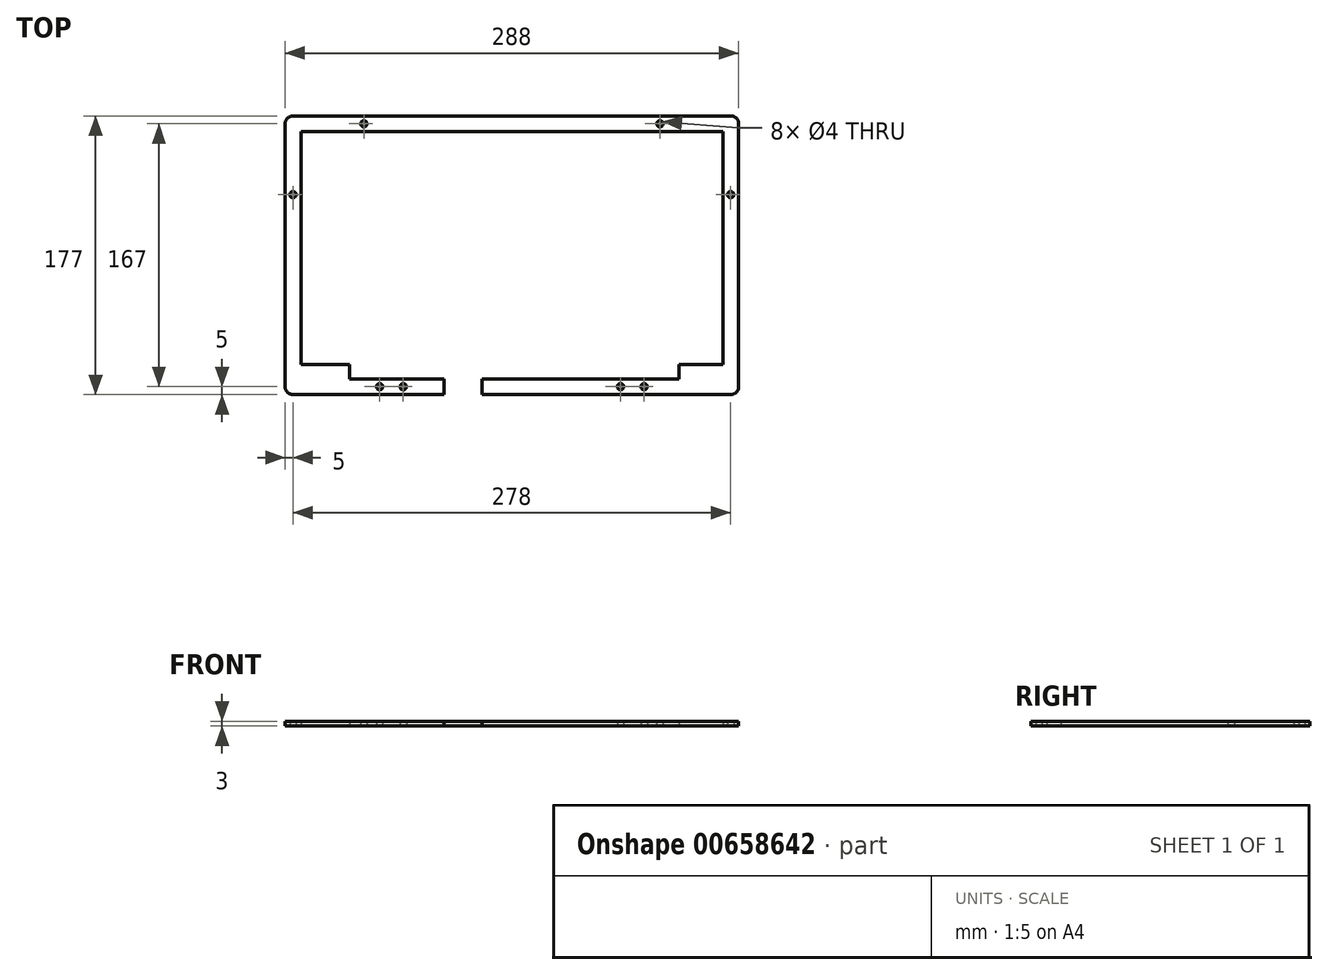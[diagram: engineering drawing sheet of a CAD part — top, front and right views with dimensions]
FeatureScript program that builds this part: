
annotation { "Feature Type Name" : "Feature", "Feature Type Description" : "" }
export const myFeature = defineFeature(function(context is Context, id is Id, definition is map)
    precondition{}
    {
        {
            var Q0;
            Q0=qCreatedBy(makeId("Top.planeOp"),FACE);
            var sketch = newSketch(context, id + "F0", { "sketchPlane" : qUnion([Q0])});
            skLineSegment(sketch, "E0.bottom", {"start": v(-144, 96) * mm, "end": v(144, 96) * mm});
            skLineSegment(sketch, "E0.top", {"start": v(-144, -81) * mm, "end": v(144, -81) * mm});
            skLineSegment(sketch, "E0.left", {"start": v(-144, 96) * mm, "end": v(-144, -81) * mm});
            skLineSegment(sketch, "E0.right", {"start": v(144, 96) * mm, "end": v(144, -81) * mm});
            skCircle(sketch, "E1", {"center": v(-94, 91) * mm, "radius": 2 * mm});
            skCircle(sketch, "E2", {"center": v(-139, 46) * mm, "radius": 2 * mm});
            skCircle(sketch, "E3", {"center": v(94, 91) * mm, "radius": 2 * mm});
            skCircle(sketch, "E4", {"center": v(139, 46) * mm, "radius": 2 * mm});
            skCircle(sketch, "E5", {"center": v(-84, -76) * mm, "radius": 2 * mm});
            skCircle(sketch, "E6", {"center": v(-69, -76) * mm, "radius": 2 * mm});
            skCircle(sketch, "E7", {"center": v(84, -76) * mm, "radius": 2 * mm});
            skCircle(sketch, "E8", {"center": v(69, -76) * mm, "radius": 2 * mm});
            skLineSegment(sketch, "E9.bottom", {"start": v(-134, 86) * mm, "end": v(134, 86) * mm});
            skLineSegment(sketch, "E9.left", {"start": v(-134, 86) * mm, "end": v(-134, -62) * mm});
            skLineSegment(sketch, "E9.right", {"start": v(134, 86) * mm, "end": v(134, -62) * mm});
            skLineSegment(sketch, "E10", {"start": v(-134, -62) * mm, "end": v(-103, -62) * mm});
            skLineSegment(sketch, "E11", {"start": v(134, -62) * mm, "end": v(106, -62) * mm});
            skLineSegment(sketch, "E12", {"start": v(-103, -62) * mm, "end": v(-103, -71) * mm});
            skLineSegment(sketch, "E13", {"start": v(-103, -71) * mm, "end": v(-43, -71) * mm});
            skLineSegment(sketch, "E14", {"start": v(-43, -71) * mm, "end": v(-43, -81) * mm});
            skLineSegment(sketch, "E15", {"start": v(106, -62) * mm, "end": v(106, -71) * mm});
            skLineSegment(sketch, "E16", {"start": v(106, -71) * mm, "end": v(-19, -71) * mm});
            skLineSegment(sketch, "E17", {"start": v(-19, -71) * mm, "end": v(-19, -81) * mm});
            skSolve(sketch);
        }
        {
            var Q0;
            Q0=makeQuery(id+"F0.imprint","IMPRINT",FACE,{"disambiguationData":[TD([[makeQuery(id+"F0.imprint","IMPRINT",EDGE,{"derivedFrom":sQuery(id+"F0.wireOp",EDGE,"E0.bottom")}),-1.0]])]});
            extrude(context, id + "F1", {"entities" : qUnion([Q0]), "depth" : 3 * mm, "offsetDistance" : 25 * mm});
        }
        {
            var Q0;
            Q0=makeQuery(id+"F1.opExtrude","SWEPT_EDGE",EDGE,{"disambiguationData":[OSD([sQuery(id+"F0.wireOp",EDGE,"E0.top"),sQuery(id+"F0.wireOp",EDGE,"E0.left")])]});
            var Q1;
            Q1=makeQuery(id+"F1.opExtrude","SWEPT_EDGE",EDGE,{"disambiguationData":[OSD([sQuery(id+"F0.wireOp",EDGE,"E0.bottom"),sQuery(id+"F0.wireOp",EDGE,"E0.left")])]});
            var Q2;
            Q2=makeQuery(id+"F1.opExtrude","SWEPT_EDGE",EDGE,{"disambiguationData":[OSD([sQuery(id+"F0.wireOp",EDGE,"E0.bottom"),sQuery(id+"F0.wireOp",EDGE,"E0.right")])]});
            var Q3;
            Q3=makeQuery(id+"F1.opExtrude","SWEPT_EDGE",EDGE,{"disambiguationData":[OSD([sQuery(id+"F0.wireOp",EDGE,"E0.top"),sQuery(id+"F0.wireOp",EDGE,"E0.right")])]});
            fillet(context, id + "F2", {"entities" : qUnion([Q0, Q1, Q2, Q3]), "radius" : 5 * mm, "tangentPropagation" : true, "allowEdgeOverflow" : false});
        }
    });
